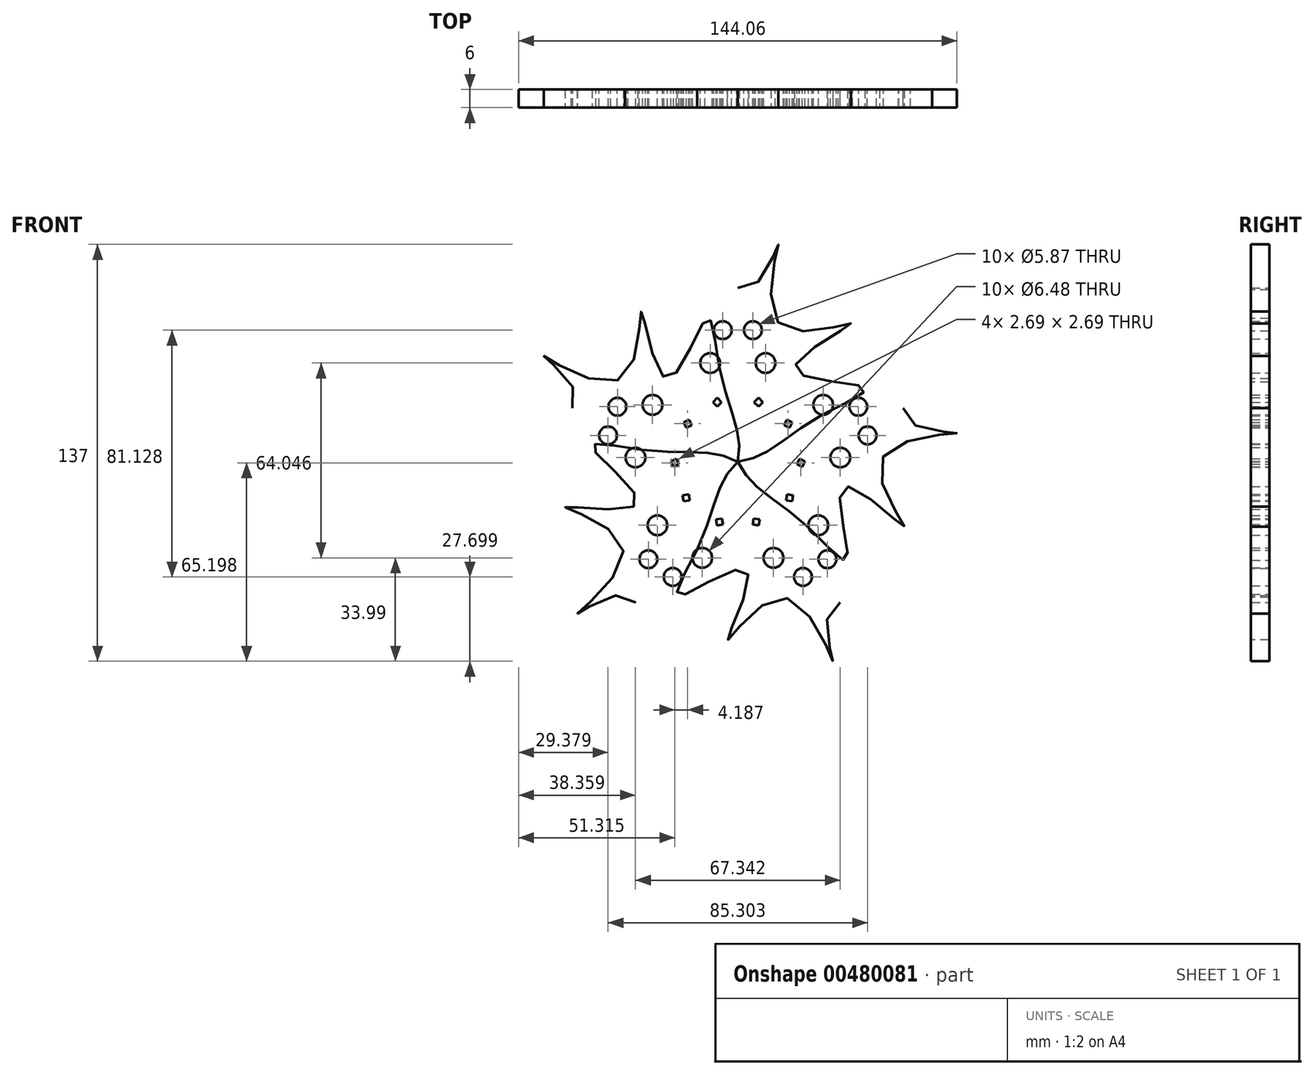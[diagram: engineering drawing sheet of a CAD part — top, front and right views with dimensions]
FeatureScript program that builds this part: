
annotation { "Feature Type Name" : "Feature", "Feature Type Description" : "" }
export const myFeature = defineFeature(function(context is Context, id is Id, definition is map)
    precondition{}
    {
        {
            var Q0;
            Q0=qCreatedBy(makeId("Front.planeOp"),FACE);
            var sketch = newSketch(context, id + "F0", { "sketchPlane" : qUnion([Q0])});
            skLineSegment(sketch, "E0", {"start": v(0, 0) * mm, "end": v(0, 57.13) * mm, "construction": true});
            skFitSpline(sketch, "E1", {"points": [v(0, 57.13) * mm, v(13.27, 71.37) * mm, v(13.66, 45.37) * mm, v(37.18, 45.37) * mm, v(18.7, 30.67) * mm, v(41.38, 24.37) * mm, v(28.78, 15.97) * mm, v(10.35, 3.8) * mm, v(0, 0) * mm], "startDerivative": vector(165.79, -101.13) * mm, "endDerivative": vector(-132.23, -18.23) * mm});
            skCircle(sketch, "E2", {"center": v(4.95, 43.24) * mm, "radius": 2.93 * mm});
            skCircle(sketch, "E3", {"center": v(9.1, 32.45) * mm, "radius": 3.24 * mm});
            skLineSegment(sketch, "E4.bottom", {"start": v(6.77, 21) * mm, "end": v(8.19, 19.58) * mm});
            skLineSegment(sketch, "E4.top", {"start": v(5.36, 19.58) * mm, "end": v(6.77, 18.17) * mm});
            skLineSegment(sketch, "E4.left", {"start": v(6.77, 21) * mm, "end": v(5.36, 19.58) * mm});
            skLineSegment(sketch, "E4.right", {"start": v(8.19, 19.58) * mm, "end": v(6.77, 18.17) * mm});
            skLineSegment(sketch, "E5.MirrorCS", {"start": v(-5.36, 19.58) * mm, "end": v(-6.77, 18.17) * mm});
            skLineSegment(sketch, "E6.MirrorCS", {"start": v(-6.77, 21) * mm, "end": v(-8.19, 19.58) * mm});
            skLineSegment(sketch, "E7.MirrorCS", {"start": v(-6.77, 21) * mm, "end": v(-5.36, 19.58) * mm});
            skLineSegment(sketch, "E8.MirrorCS", {"start": v(-8.19, 19.58) * mm, "end": v(-6.77, 18.17) * mm});
            skCircle(sketch, "E9.MirrorC", {"center": v(-9.1, 32.45) * mm, "radius": 3.24 * mm});
            skCircle(sketch, "E10.MirrorC", {"center": v(-4.95, 43.24) * mm, "radius": 2.93 * mm});
            skFitSpline(sketch, "E11.MirrorCS", {"points": [v(0, 57.13) * mm, v(-13.27, 71.37) * mm, v(-13.66, 45.37) * mm, v(-37.18, 45.37) * mm, v(-18.7, 30.67) * mm, v(-41.38, 24.37) * mm, v(-28.78, 15.97) * mm, v(-10.35, 3.8) * mm, v(0, 0) * mm], "startDerivative": vector(-165.79, -101.13) * mm, "endDerivative": vector(132.23, -18.23) * mm});
            skSolve(sketch);
        }
        {
            var Q0;
            Q0 = qSketchRegion(id + "F0", true);
            extrude(context, id + "F1", {"entities" : qUnion([Q0]), "depth" : 6 * mm});
        }
        {
            var Q0;
            Q0=qCreatedBy(makeId("Right.planeOp"),FACE);
            var sketch = newSketch(context, id + "F2", { "sketchPlane" : qUnion([Q0])});
            skLineSegment(sketch, "E12", {"start": v(0, 0) * mm, "end": v(-62.32, 0) * mm, "construction": true});
            skSolve(sketch);
        }
        {
            var Q0;
            Q0=makeQuery(id+"F1.opExtrude","SWEPT_BODY",BODY,{"disambiguationData":[OSD([sQuery(id+"F0.wireOp",EDGE,"E1"),sQuery(id+"F0.wireOp",EDGE,"E2"),sQuery(id+"F0.wireOp",EDGE,"E3"),sQuery(id+"F0.wireOp",EDGE,"E4.bottom"),sQuery(id+"F0.wireOp",EDGE,"E4.top"),sQuery(id+"F0.wireOp",EDGE,"E4.left"),sQuery(id+"F0.wireOp",EDGE,"E4.right"),sQuery(id+"F0.wireOp",EDGE,"E5.MirrorCS"),sQuery(id+"F0.wireOp",EDGE,"E6.MirrorCS"),sQuery(id+"F0.wireOp",EDGE,"E7.MirrorCS"),sQuery(id+"F0.wireOp",EDGE,"E8.MirrorCS"),sQuery(id+"F0.wireOp",EDGE,"E9.MirrorC"),sQuery(id+"F0.wireOp",EDGE,"E10.MirrorC"),sQuery(id+"F0.wireOp",EDGE,"E11.MirrorCS")])]});
            var Q1;
            Q1=sQuery(id+"F2.wireOp",EDGE,"E12");
            circularPattern(context, id + "F3", {"entities" : qUnion([Q0]), "axis" : qUnion([Q1]), "angle" : 360 * degree, "instanceCount" : 5, "oppositeDirection" : true, "equalSpace" : true});
        }
    });
